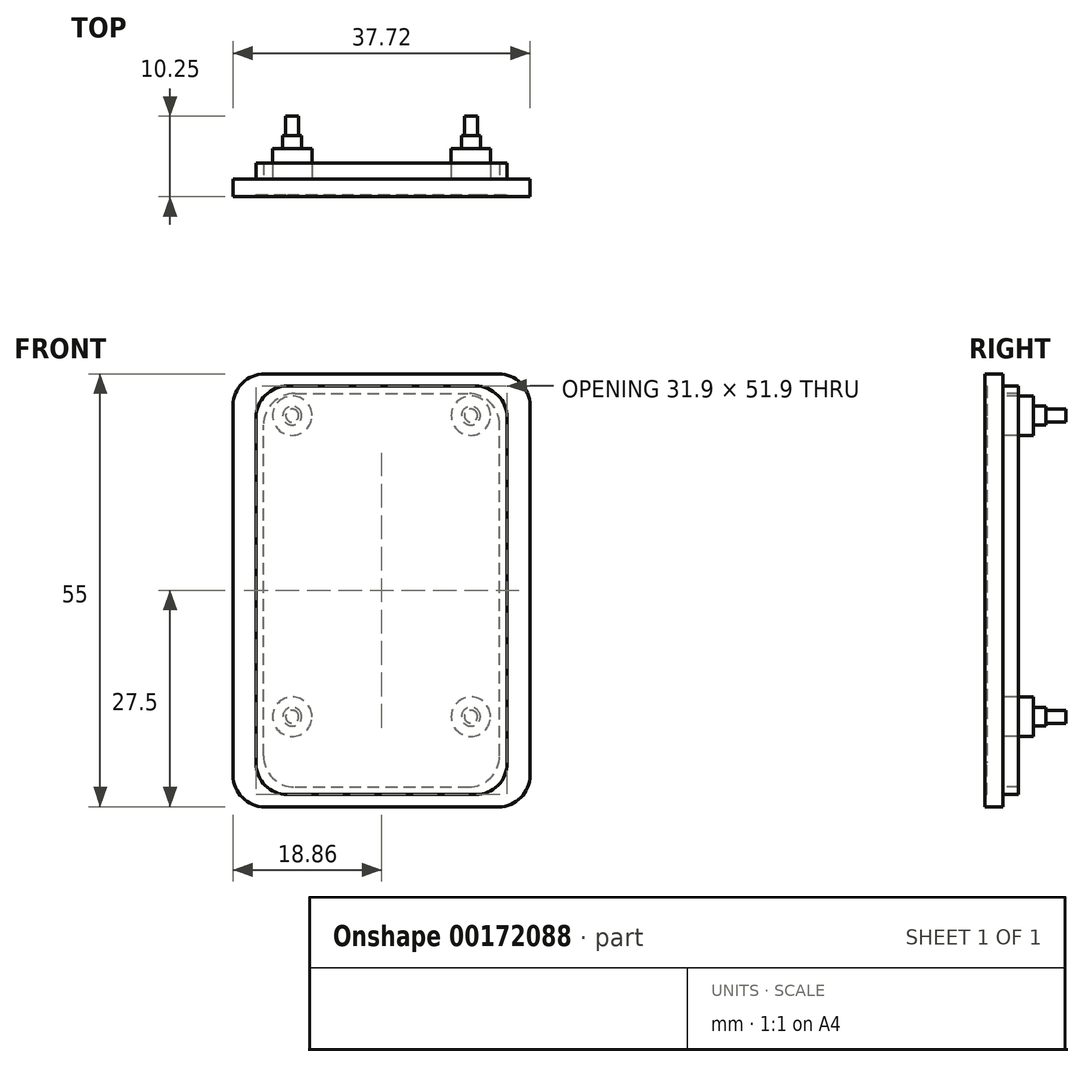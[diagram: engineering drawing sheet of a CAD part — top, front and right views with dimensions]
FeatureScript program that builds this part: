
annotation { "Feature Type Name" : "Feature", "Feature Type Description" : "" }
export const myFeature = defineFeature(function(context is Context, id is Id, definition is map)
    precondition{}
    {
        {
            var Q0;
            Q0=qCreatedBy(makeId("Front.planeOp"),FACE);
            var sketch = newSketch(context, id + "F0", { "sketchPlane" : qUnion([Q0])});
            skLineSegment(sketch, "E0.bottom", {"start": v(11.95, -25.95) * mm, "end": v(-11.95, -25.95) * mm});
            skLineSegment(sketch, "E0.top", {"start": v(11.95, 25.95) * mm, "end": v(-11.95, 25.95) * mm});
            skLineSegment(sketch, "E0.left", {"start": v(15.95, -21.95) * mm, "end": v(15.95, 21.95) * mm});
            skLineSegment(sketch, "E0.right", {"start": v(-15.95, -21.95) * mm, "end": v(-15.95, 21.95) * mm});
            skPoint(sketch, "E0.middle", {"position": v(0, 0) * mm});
            skPoint(sketch, "E1.visualSharp", {"position": v(-15.95, 25.95) * mm});
            skArc(sketch, "E1.filletArc", {"start": v(-11.95, 25.95) * mm, "mid": v(-14.78, 24.78) * mm, "end": v(-15.95, 21.95) * mm});
            skPoint(sketch, "E2.visualSharp", {"position": v(15.95, 25.95) * mm});
            skArc(sketch, "E2.filletArc", {"start": v(15.95, 21.95) * mm, "mid": v(14.78, 24.78) * mm, "end": v(11.95, 25.95) * mm});
            skPoint(sketch, "E3.visualSharp", {"position": v(15.95, -25.95) * mm});
            skArc(sketch, "E3.filletArc", {"start": v(11.95, -25.95) * mm, "mid": v(14.78, -24.78) * mm, "end": v(15.95, -21.95) * mm});
            skPoint(sketch, "E4.visualSharp", {"position": v(-15.95, -25.95) * mm});
            skArc(sketch, "E4.filletArc", {"start": v(-15.95, -21.95) * mm, "mid": v(-14.78, -24.78) * mm, "end": v(-11.95, -25.95) * mm});
            skLineSegment(sketch, "E5.bottom", {"start": v(14.86, -27.5) * mm, "end": v(-14.86, -27.5) * mm});
            skLineSegment(sketch, "E5.top", {"start": v(14.86, 27.5) * mm, "end": v(-14.86, 27.5) * mm});
            skLineSegment(sketch, "E5.left", {"start": v(18.86, -23.5) * mm, "end": v(18.86, 23.5) * mm});
            skLineSegment(sketch, "E5.right", {"start": v(-18.86, -23.5) * mm, "end": v(-18.86, 23.5) * mm});
            skPoint(sketch, "E6.visualSharp", {"position": v(-18.86, 27.5) * mm});
            skArc(sketch, "E6.filletArc", {"start": v(-14.86, 27.5) * mm, "mid": v(-17.69, 26.33) * mm, "end": v(-18.86, 23.5) * mm});
            skPoint(sketch, "E7.visualSharp", {"position": v(18.86, 27.5) * mm});
            skArc(sketch, "E7.filletArc", {"start": v(18.86, 23.5) * mm, "mid": v(17.69, 26.33) * mm, "end": v(14.86, 27.5) * mm});
            skPoint(sketch, "E8.visualSharp", {"position": v(18.86, -27.5) * mm});
            skArc(sketch, "E8.filletArc", {"start": v(14.86, -27.5) * mm, "mid": v(17.69, -26.33) * mm, "end": v(18.86, -23.5) * mm});
            skPoint(sketch, "E9.visualSharp", {"position": v(-18.86, -27.5) * mm});
            skArc(sketch, "E9.filletArc", {"start": v(-18.86, -23.5) * mm, "mid": v(-17.69, -26.33) * mm, "end": v(-14.86, -27.5) * mm});
            skCircle(sketch, "E10", {"center": v(-11.35, 22.2) * mm, "radius": 1.2 * mm});
            skLineSegment(sketch, "E11", {"start": v(0, 47.27) * mm, "end": v(0, -48.1) * mm});
            skCircle(sketch, "E12", {"center": v(11.35, 22.2) * mm, "radius": 1.2 * mm});
            skCircle(sketch, "E13", {"center": v(-11.35, -16.05) * mm, "radius": 1.2 * mm});
            skCircle(sketch, "E14", {"center": v(11.35, -16.05) * mm, "radius": 1.2 * mm});
            skCircle(sketch, "E15", {"center": v(11.35, 22.2) * mm, "radius": 2.5 * mm});
            skCircle(sketch, "E16", {"center": v(-11.35, 22.2) * mm, "radius": 2.5 * mm});
            skCircle(sketch, "E17", {"center": v(-11.35, -16.05) * mm, "radius": 2.5 * mm});
            skCircle(sketch, "E18", {"center": v(11.35, -16.05) * mm, "radius": 2.5 * mm});
            skCircle(sketch, "E19", {"center": v(-11.35, 22.2) * mm, "radius": 0.82 * mm});
            skCircle(sketch, "E20", {"center": v(11.35, 22.2) * mm, "radius": 0.82 * mm});
            skCircle(sketch, "E21", {"center": v(11.35, -16.05) * mm, "radius": 0.82 * mm});
            skCircle(sketch, "E22", {"center": v(-11.35, -16.05) * mm, "radius": 0.82 * mm});
            skLineSegment(sketch, "E23.bottom", {"start": v(-11, -25) * mm, "end": v(11, -25) * mm});
            skLineSegment(sketch, "E23.top", {"start": v(-11, 25) * mm, "end": v(11, 25) * mm});
            skLineSegment(sketch, "E23.left", {"start": v(-15, -21) * mm, "end": v(-15, 21) * mm});
            skLineSegment(sketch, "E23.right", {"start": v(15, -21) * mm, "end": v(15, 21) * mm});
            skPoint(sketch, "E24.visualSharp", {"position": v(-15, 25) * mm});
            skArc(sketch, "E24.filletArc", {"start": v(-11, 25) * mm, "mid": v(-13.83, 23.83) * mm, "end": v(-15, 21) * mm});
            skPoint(sketch, "E25.visualSharp", {"position": v(15, 25) * mm});
            skArc(sketch, "E25.filletArc", {"start": v(15, 21) * mm, "mid": v(13.83, 23.83) * mm, "end": v(11, 25) * mm});
            skPoint(sketch, "E26.visualSharp", {"position": v(-15, -25) * mm});
            skArc(sketch, "E26.filletArc", {"start": v(-15, -21) * mm, "mid": v(-13.83, -23.83) * mm, "end": v(-11, -25) * mm});
            skPoint(sketch, "E27.visualSharp", {"position": v(15, -25) * mm});
            skArc(sketch, "E27.filletArc", {"start": v(11, -25) * mm, "mid": v(13.83, -23.83) * mm, "end": v(15, -21) * mm});
            skLineSegment(sketch, "E28", {"start": v(15.95, 15) * mm, "end": v(15, 15) * mm});
            skLineSegment(sketch, "E29", {"start": v(-15, 15) * mm, "end": v(-15.95, 15) * mm});
            skLineSegment(sketch, "E30", {"start": v(15.95, -15) * mm, "end": v(15, -15) * mm});
            skLineSegment(sketch, "E31", {"start": v(-15, -15) * mm, "end": v(-15.95, -15) * mm});
            skSolve(sketch);
        }
        {
            var Q0;
            Q0=makeQuery(id+"F0.imprint","IMPRINT",FACE,{"disambiguationData":[TD([[makeQuery(id+"F0.imprint","IMPRINT",EDGE,{"derivedFrom":sQuery(id+"F0.wireOp",EDGE,"E14")}),-1.0]])]});
            var Q1;
            Q1=makeQuery(id+"F0.imprint","IMPRINT",FACE,{"disambiguationData":[TD([[makeQuery(id+"F0.imprint","IMPRINT",EDGE,{"derivedFrom":sQuery(id+"F0.wireOp",EDGE,"E13")}),-1.0]])]});
            var Q2;
            Q2=makeQuery(id+"F0.imprint","IMPRINT",FACE,{"disambiguationData":[TD([[makeQuery(id+"F0.imprint","IMPRINT",EDGE,{"derivedFrom":sQuery(id+"F0.wireOp",EDGE,"E12")}),-1.0]])]});
            var Q3;
            Q3=makeQuery(id+"F0.imprint","IMPRINT",FACE,{"disambiguationData":[TD([[makeQuery(id+"F0.imprint","IMPRINT",EDGE,{"derivedFrom":sQuery(id+"F0.wireOp",EDGE,"E10")}),-1.0]])]});
            var Q4;
            {var subQ0=sQuery(id+"F0.wireOp",EDGE,"E1.filletArc");Q4=makeQuery(id+"F0.imprint","IMPRINT",FACE,{"disambiguationData":[TD([[makeQuery(id+"F0.imprint","IMPRINT",EDGE,{"derivedFrom":subQ0}),-1.0]])]});}
            var Q5;
            {var subQ0=sQuery(id+"F0.wireOp",EDGE,"E2.filletArc");Q5=makeQuery(id+"F0.imprint","IMPRINT",FACE,{"disambiguationData":[TD([[makeQuery(id+"F0.imprint","IMPRINT",EDGE,{"derivedFrom":subQ0}),-1.0]])]});}
            var Q6;
            {var subQ0=sQuery(id+"F0.wireOp",EDGE,"E28");Q6=makeQuery(id+"F0.imprint","IMPRINT",FACE,{"disambiguationData":[TD([[makeQuery(id+"F0.imprint","IMPRINT",EDGE,{"derivedFrom":subQ0}),1.0]])]});}
            var Q7;
            {var subQ0=sQuery(id+"F0.wireOp",EDGE,"E29");Q7=makeQuery(id+"F0.imprint","IMPRINT",FACE,{"disambiguationData":[TD([[makeQuery(id+"F0.imprint","IMPRINT",EDGE,{"derivedFrom":subQ0}),1.0]])]});}
            var Q8;
            Q8=makeQuery(id+"F0.imprint","IMPRINT",FACE,{"disambiguationData":[TD([[makeQuery(id+"F0.imprint","IMPRINT",EDGE,{"derivedFrom":sQuery(id+"F0.wireOp",EDGE,"E13")}),1.0]])]});
            var Q9;
            Q9=makeQuery(id+"F0.imprint","IMPRINT",FACE,{"disambiguationData":[TD([[makeQuery(id+"F0.imprint","IMPRINT",EDGE,{"derivedFrom":sQuery(id+"F0.wireOp",EDGE,"E12")}),1.0]])]});
            var Q10;
            Q10=makeQuery(id+"F0.imprint","IMPRINT",FACE,{"disambiguationData":[TD([[makeQuery(id+"F0.imprint","IMPRINT",EDGE,{"derivedFrom":sQuery(id+"F0.wireOp",EDGE,"E10")}),1.0]])]});
            var Q11;
            Q11=makeQuery(id+"F0.imprint","IMPRINT",FACE,{"disambiguationData":[TD([[makeQuery(id+"F0.imprint","IMPRINT",EDGE,{"derivedFrom":sQuery(id+"F0.wireOp",EDGE,"E14")}),1.0]])]});
            var Q12;
            Q12=makeQuery(id+"F0.imprint","IMPRINT",FACE,{"disambiguationData":[TD([[makeQuery(id+"F0.imprint","IMPRINT",EDGE,{"derivedFrom":sQuery(id+"F0.wireOp",EDGE,"E22")}),1.0]])]});
            var Q13;
            Q13=makeQuery(id+"F0.imprint","IMPRINT",FACE,{"disambiguationData":[TD([[makeQuery(id+"F0.imprint","IMPRINT",EDGE,{"derivedFrom":sQuery(id+"F0.wireOp",EDGE,"E21")}),1.0]])]});
            var Q14;
            Q14=makeQuery(id+"F0.imprint","IMPRINT",FACE,{"disambiguationData":[TD([[makeQuery(id+"F0.imprint","IMPRINT",EDGE,{"derivedFrom":sQuery(id+"F0.wireOp",EDGE,"E20")}),1.0]])]});
            var Q15;
            Q15=makeQuery(id+"F0.imprint","IMPRINT",FACE,{"disambiguationData":[TD([[makeQuery(id+"F0.imprint","IMPRINT",EDGE,{"derivedFrom":sQuery(id+"F0.wireOp",EDGE,"E19")}),1.0]])]});
            var Q16;
            Q16=makeQuery(id+"F0.imprint","IMPRINT",FACE,{"disambiguationData":[TD([[makeQuery(id+"F0.imprint","IMPRINT",EDGE,{"derivedFrom":sQuery(id+"F0.wireOp",EDGE,"E15")}),-1.0]])]});
            var Q17;
            Q17=makeQuery(id+"F0.imprint","IMPRINT",FACE,{"disambiguationData":[TD([[makeQuery(id+"F0.imprint","IMPRINT",EDGE,{"derivedFrom":sQuery(id+"F0.wireOp",EDGE,"E16")}),-1.0]])]});
            var Q18;
            {var subQ5=sQuery(id+"F0.wireOp",EDGE,"E1.filletArc");Q18=makeQuery(id+"F0.imprint","IMPRINT",FACE,{"disambiguationData":[TD([[makeQuery(id+"F0.imprint","IMPRINT",EDGE,{"derivedFrom":subQ5}),1.0]])]});}
            var Q19;
            {var subQ5=sQuery(id+"F0.wireOp",EDGE,"E2.filletArc");Q19=makeQuery(id+"F0.imprint","IMPRINT",FACE,{"disambiguationData":[TD([[makeQuery(id+"F0.imprint","IMPRINT",EDGE,{"derivedFrom":subQ5}),1.0]])]});}
            var Q20;
            {var subQ5=sQuery(id+"F0.wireOp",EDGE,"E3.filletArc");Q20=makeQuery(id+"F0.imprint","IMPRINT",FACE,{"disambiguationData":[TD([[makeQuery(id+"F0.imprint","IMPRINT",EDGE,{"derivedFrom":subQ5}),1.0]])]});}
            var Q21;
            {var subQ5=sQuery(id+"F0.wireOp",EDGE,"E4.filletArc");Q21=makeQuery(id+"F0.imprint","IMPRINT",FACE,{"disambiguationData":[TD([[makeQuery(id+"F0.imprint","IMPRINT",EDGE,{"derivedFrom":subQ5}),1.0]])]});}
            extrude(context, id + "F1", {"entities" : qUnion([Q0, Q1, Q2, Q3, Q4, Q5, Q6, Q7, Q8, Q9, Q10, Q11, Q12, Q13, Q14, Q15, Q16, Q17, Q18, Q19, Q20, Q21]), "depth" : 2 * mm});
        }
        {
            var Q0;
            Q0=makeQuery(id+"F0.imprint","IMPRINT",FACE,{"disambiguationData":[TD([[makeQuery(id+"F0.imprint","IMPRINT",EDGE,{"derivedFrom":sQuery(id+"F0.wireOp",EDGE,"E0.left")}),1.0]])]});
            var Q1;
            {var subQ0=sQuery(id+"F0.wireOp",EDGE,"6KJQdiIa-Go68-Vb6l-QF9a-gq7Ak1E7ayVD");Q1=makeQuery(id+"F0.imprint","IMPRINT",FACE,{"disambiguationData":[TD([[makeQuery(id+"F0.imprint","IMPRINT",EDGE,{"derivedFrom":subQ0}),-1.0]])]});}
            var Q2;
            {var subQ0=sQuery(id+"F0.wireOp",EDGE,"QE6DL7wR-UIWS-2v5Q-kbow-E4hswlpKnxd8");Q2=makeQuery(id+"F0.imprint","IMPRINT",FACE,{"disambiguationData":[TD([[makeQuery(id+"F0.imprint","IMPRINT",EDGE,{"derivedFrom":subQ0}),1.0]])]});}
            var Q3;
            Q3=makeQuery(id+"F0.imprint","IMPRINT",FACE,{"disambiguationData":[TD([[makeQuery(id+"F0.imprint","IMPRINT",EDGE,{"derivedFrom":sQuery(id+"F0.wireOp",EDGE,"E0.right")}),-1.0]])]});
            var Q4;
            {var subQ0=sQuery(id+"F0.wireOp",EDGE,"cDHgHE3r-5zVM-ukHL-wcK1-OFUA43IhbbjD");Q4=makeQuery(id+"F0.imprint","IMPRINT",FACE,{"disambiguationData":[TD([[makeQuery(id+"F0.imprint","IMPRINT",EDGE,{"derivedFrom":subQ0}),-1.0]])]});}
            var Q5;
            {var subQ0=sQuery(id+"F0.wireOp",EDGE,"2W9BhyVd-kjhX-L4Qu-GEE9-STJ9oPLwQMcy");Q5=makeQuery(id+"F0.imprint","IMPRINT",FACE,{"disambiguationData":[TD([[makeQuery(id+"F0.imprint","IMPRINT",EDGE,{"derivedFrom":subQ0}),1.0]])]});}
            var Q6;
            {var subQ5=sQuery(id+"F0.wireOp",EDGE,"E2.filletArc");Q6=makeQuery(id+"F0.imprint","IMPRINT",FACE,{"disambiguationData":[TD([[makeQuery(id+"F0.imprint","IMPRINT",EDGE,{"derivedFrom":subQ5}),1.0]])]});}
            var Q7;
            {var subQ5=sQuery(id+"F0.wireOp",EDGE,"E1.filletArc");Q7=makeQuery(id+"F0.imprint","IMPRINT",FACE,{"disambiguationData":[TD([[makeQuery(id+"F0.imprint","IMPRINT",EDGE,{"derivedFrom":subQ5}),1.0]])]});}
            var Q8;
            {var subQ5=sQuery(id+"F0.wireOp",EDGE,"E4.filletArc");Q8=makeQuery(id+"F0.imprint","IMPRINT",FACE,{"disambiguationData":[TD([[makeQuery(id+"F0.imprint","IMPRINT",EDGE,{"derivedFrom":subQ5}),1.0]])]});}
            var Q9;
            {var subQ5=sQuery(id+"F0.wireOp",EDGE,"E3.filletArc");Q9=makeQuery(id+"F0.imprint","IMPRINT",FACE,{"disambiguationData":[TD([[makeQuery(id+"F0.imprint","IMPRINT",EDGE,{"derivedFrom":subQ5}),1.0]])]});}
            extrude(context, id + "F2", {"entities" : qUnion([Q0, Q1, Q2, Q3, Q4, Q5, Q6, Q7, Q8, Q9]), "operationType" : NewBodyOperationType.ADD, "oppositeDirection" : true, "depth" : 2 * mm});
        }
        {
            var Q0;
            {var subQ0=sQuery(id+"F0.wireOp",EDGE,"E2.filletArc");Q0=makeQuery(id+"F0.imprint","IMPRINT",FACE,{"disambiguationData":[TD([[makeQuery(id+"F0.imprint","IMPRINT",EDGE,{"derivedFrom":subQ0}),-1.0]])]});}
            var Q1;
            {var subQ0=sQuery(id+"F0.wireOp",EDGE,"E1.filletArc");Q1=makeQuery(id+"F0.imprint","IMPRINT",FACE,{"disambiguationData":[TD([[makeQuery(id+"F0.imprint","IMPRINT",EDGE,{"derivedFrom":subQ0}),-1.0]])]});}
            extrude(context, id + "F3", {"entities" : qUnion([Q0, Q1]), "operationType" : NewBodyOperationType.ADD, "depth" : 2.25 * mm});
        }
        {
            var Q0;
            Q0=makeQuery(id+"F0.imprint","IMPRINT",FACE,{"disambiguationData":[TD([[makeQuery(id+"F0.imprint","IMPRINT",EDGE,{"derivedFrom":sQuery(id+"F0.wireOp",EDGE,"E21")}),1.0]])]});
            var Q1;
            Q1=makeQuery(id+"F0.imprint","IMPRINT",FACE,{"disambiguationData":[TD([[makeQuery(id+"F0.imprint","IMPRINT",EDGE,{"derivedFrom":sQuery(id+"F0.wireOp",EDGE,"E22")}),1.0]])]});
            var Q2;
            Q2=makeQuery(id+"F0.imprint","IMPRINT",FACE,{"disambiguationData":[TD([[makeQuery(id+"F0.imprint","IMPRINT",EDGE,{"derivedFrom":sQuery(id+"F0.wireOp",EDGE,"E19")}),1.0]])]});
            var Q3;
            Q3=makeQuery(id+"F0.imprint","IMPRINT",FACE,{"disambiguationData":[TD([[makeQuery(id+"F0.imprint","IMPRINT",EDGE,{"derivedFrom":sQuery(id+"F0.wireOp",EDGE,"E20")}),1.0]])]});
            extrude(context, id + "F4", {"entities" : qUnion([Q0, Q1, Q2, Q3]), "operationType" : NewBodyOperationType.ADD, "oppositeDirection" : true, "depth" : 8 * mm});
        }
        {
            var Q0;
            Q0=makeQuery(id+"F0.imprint","IMPRINT",FACE,{"disambiguationData":[TD([[makeQuery(id+"F0.imprint","IMPRINT",EDGE,{"derivedFrom":sQuery(id+"F0.wireOp",EDGE,"E14")}),1.0]])]});
            var Q1;
            Q1=makeQuery(id+"F0.imprint","IMPRINT",FACE,{"disambiguationData":[TD([[makeQuery(id+"F0.imprint","IMPRINT",EDGE,{"derivedFrom":sQuery(id+"F0.wireOp",EDGE,"E13")}),1.0]])]});
            var Q2;
            Q2=makeQuery(id+"F0.imprint","IMPRINT",FACE,{"disambiguationData":[TD([[makeQuery(id+"F0.imprint","IMPRINT",EDGE,{"derivedFrom":sQuery(id+"F0.wireOp",EDGE,"E10")}),1.0]])]});
            var Q3;
            Q3=makeQuery(id+"F0.imprint","IMPRINT",FACE,{"disambiguationData":[TD([[makeQuery(id+"F0.imprint","IMPRINT",EDGE,{"derivedFrom":sQuery(id+"F0.wireOp",EDGE,"E12")}),1.0]])]});
            extrude(context, id + "F5", {"entities" : qUnion([Q0, Q1, Q2, Q3]), "operationType" : NewBodyOperationType.ADD, "oppositeDirection" : true, "depth" : 5.5 * mm});
        }
        {
            var Q0;
            Q0=makeQuery(id+"F0.imprint","IMPRINT",FACE,{"disambiguationData":[TD([[makeQuery(id+"F0.imprint","IMPRINT",EDGE,{"derivedFrom":sQuery(id+"F0.wireOp",EDGE,"E12")}),-1.0]])]});
            var Q1;
            Q1=makeQuery(id+"F0.imprint","IMPRINT",FACE,{"disambiguationData":[TD([[makeQuery(id+"F0.imprint","IMPRINT",EDGE,{"derivedFrom":sQuery(id+"F0.wireOp",EDGE,"E10")}),-1.0]])]});
            var Q2;
            Q2=makeQuery(id+"F0.imprint","IMPRINT",FACE,{"disambiguationData":[TD([[makeQuery(id+"F0.imprint","IMPRINT",EDGE,{"derivedFrom":sQuery(id+"F0.wireOp",EDGE,"E14")}),-1.0]])]});
            var Q3;
            Q3=makeQuery(id+"F0.imprint","IMPRINT",FACE,{"disambiguationData":[TD([[makeQuery(id+"F0.imprint","IMPRINT",EDGE,{"derivedFrom":sQuery(id+"F0.wireOp",EDGE,"E13")}),-1.0]])]});
            extrude(context, id + "F6", {"entities" : qUnion([Q0, Q1, Q2, Q3]), "operationType" : NewBodyOperationType.ADD, "oppositeDirection" : true, "depth" : 3.9 * mm});
        }
    });
